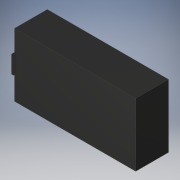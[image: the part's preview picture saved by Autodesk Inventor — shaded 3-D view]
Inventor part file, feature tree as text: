
AUTODESK INVENTOR PART (.ipt)
format: ipt  version: 2019 (Build 230136000, 136)  size: 122,368 bytes
history: native  units: mm
features: extrude x2, sketch x2, projected_geometry x1
ambient origin geometry x8: Origin, YZ Plane, XZ Plane, XY Plane, X Axis, Y Axis, Z Axis, Center Point
bodies: Solid1 (feature_tree), Body1 (feature_tree)
feature tree (5):
  extrude  "Extrusion2"  Depth=3.0mm
  extrude  "Extrusion3"  Depth=1.0mm TaperAngle=0.0deg
  sketch  "Sketch2"  dims[d2=15.0mm d3=0.0mm d5=3.0mm]
  projected_geometry  "Projected Loop2"
  sketch  "Sketch3"  dims[d6=8.0mm d7=1.0mm d8=0.0mm d9=12.5mm]
